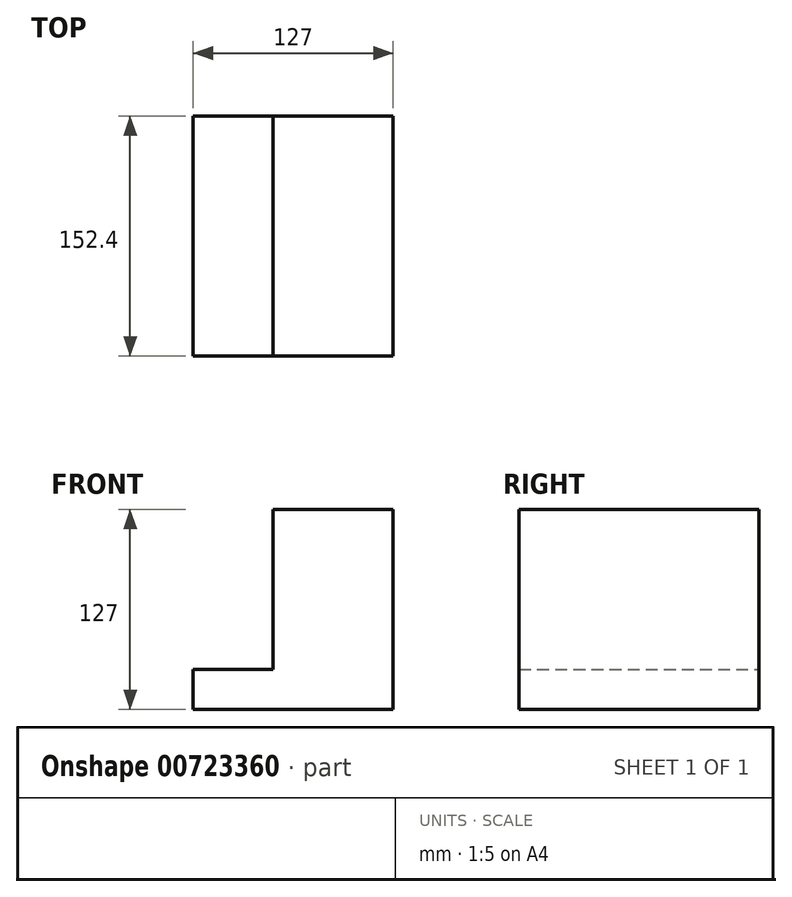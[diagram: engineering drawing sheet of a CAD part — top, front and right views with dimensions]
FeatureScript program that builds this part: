
annotation { "Feature Type Name" : "Feature", "Feature Type Description" : "" }
export const myFeature = defineFeature(function(context is Context, id is Id, definition is map)
    precondition{}
    {
        {
            var Q0;
            Q0=qCreatedBy(makeId("Front.planeOp"),FACE);
            var sketch = newSketch(context, id + "F0", { "sketchPlane" : qUnion([Q0])});
            skLineSegment(sketch, "E0", {"start": v(-82.91, -44.43) * mm, "end": v(44.09, -44.43) * mm});
            skLineSegment(sketch, "E1", {"start": v(44.09, -44.43) * mm, "end": v(44.09, 82.57) * mm});
            skLineSegment(sketch, "E2", {"start": v(44.09, 82.57) * mm, "end": v(-32.11, 82.57) * mm});
            skLineSegment(sketch, "E3", {"start": v(-32.11, 82.57) * mm, "end": v(-32.11, -19.03) * mm});
            skLineSegment(sketch, "E4", {"start": v(-32.11, -19.03) * mm, "end": v(-82.91, -19.03) * mm});
            skLineSegment(sketch, "E5", {"start": v(-82.91, -19.03) * mm, "end": v(-82.91, -44.43) * mm});
            skSolve(sketch);
        }
        {
            var Q0;
            Q0=makeQuery(id+"F0.imprint","IMPRINT",FACE,{"disambiguationData":[TD([[makeQuery(id+"F0.imprint","IMPRINT",EDGE,{"derivedFrom":sQuery(id+"F0.wireOp",EDGE,"E0")}),1.0]])]});
            extrude(context, id + "F1", {"entities" : qUnion([Q0]), "depth" : 152.4 * mm, "offsetDistance" : 25.4 * mm});
        }
    });
